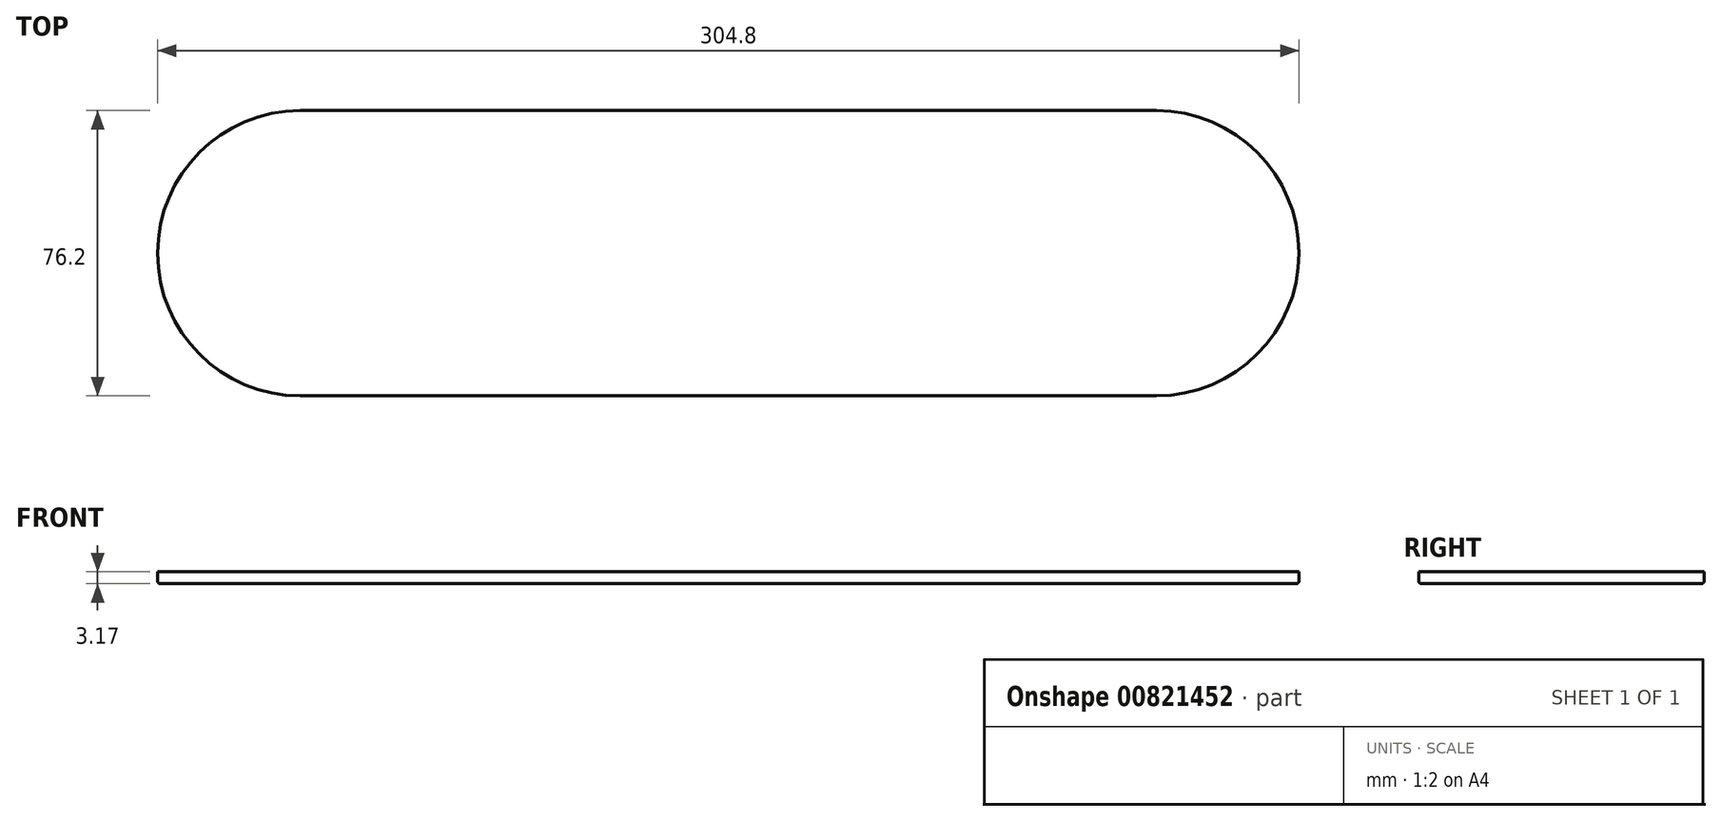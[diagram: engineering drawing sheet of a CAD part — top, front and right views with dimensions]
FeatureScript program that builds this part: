
annotation { "Feature Type Name" : "Feature", "Feature Type Description" : "" }
export const myFeature = defineFeature(function(context is Context, id is Id, definition is map)
    precondition{}
    {
        {
            var Q0;
            Q0=qCreatedBy(makeId("Top.planeOp"),FACE);
            var sketch = newSketch(context, id + "F0", { "sketchPlane" : qUnion([Q0])});
            skArc(sketch, "E0", {"start": v(0, 38.1) * mm, "mid": v(-38.1, 0) * mm, "end": v(0, -38.1) * mm});
            skArc(sketch, "E1", {"start": v(228.6, -38.1) * mm, "mid": v(266.7, 0) * mm, "end": v(228.6, 38.1) * mm});
            skLineSegment(sketch, "E2", {"start": v(0, 38.1) * mm, "end": v(228.6, 38.1) * mm});
            skLineSegment(sketch, "E3", {"start": v(228.6, -38.1) * mm, "end": v(0, -38.1) * mm});
            skSolve(sketch);
        }
        {
            var Q0;
            Q0 = qSketchRegion(id + "F0", true);
            extrude(context, id + "F1", {"entities" : qUnion([Q0]), "depth" : 3.17 * mm, "offsetDistance" : 25.4 * mm});
        }
        {
            var Q0;
            Q0=makeQuery(id+"F1.opExtrude","CAP_FACE",FACE,{"disambiguationData":[OSD([sQuery(id+"F0.wireOp",EDGE,"E0"),sQuery(id+"F0.wireOp",EDGE,"E1"),sQuery(id+"F0.wireOp",EDGE,"E2"),sQuery(id+"F0.wireOp",EDGE,"E3")])],"isStart":true});
            fillet(context, id + "F2", {"entities" : qUnion([Q0]), "radius" : 0.8 * mm, "tangentPropagation" : true, "allowEdgeOverflow" : false});
        }
    });
